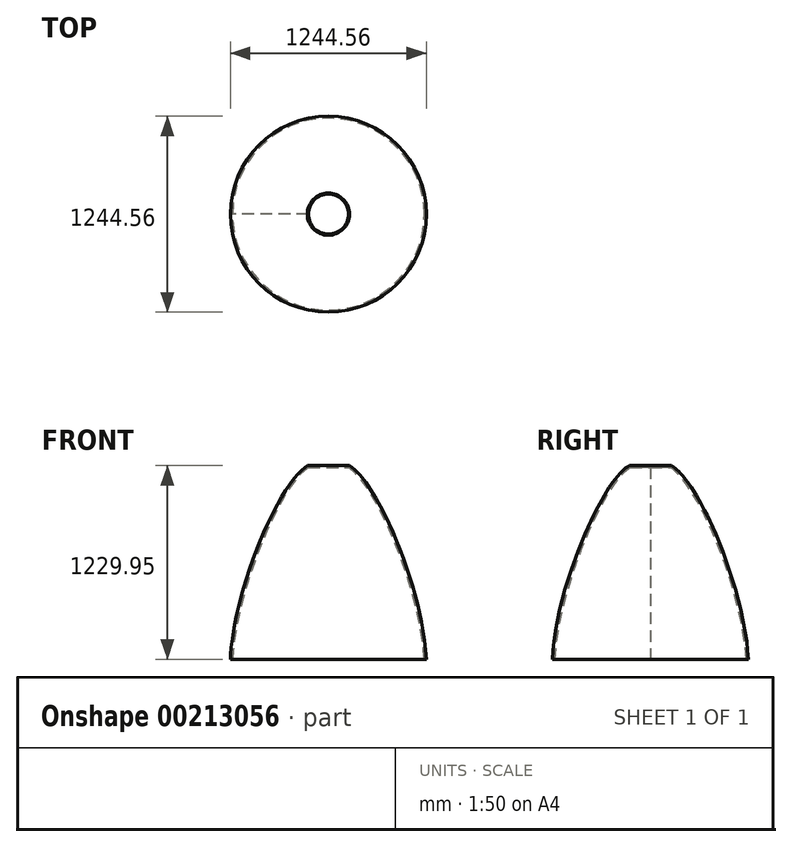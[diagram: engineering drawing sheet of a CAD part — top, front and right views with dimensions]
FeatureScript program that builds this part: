
annotation { "Feature Type Name" : "Feature", "Feature Type Description" : "" }
export const myFeature = defineFeature(function(context is Context, id is Id, definition is map)
    precondition{}
    {
        {
            var Q0;
            Q0=qCreatedBy(makeId("Front.planeOp"),FACE);
            var sketch = newSketch(context, id + "F0", { "sketchPlane" : qUnion([Q0])});
            skFitSpline(sketch, "E0", {"points": [v(-127, 0) * mm, v(-609.6, -1219.2) * mm], "startDerivative": vector(-564.76, -355.02) * mm, "endDerivative": vector(-64.8, -1241.7) * mm});
            skFitSpline(sketch, "E1.0", {"points": [v(-133.76, 10.75) * mm, v(-140.08, 6.78) * mm, v(-152.75, -2.27) * mm, v(-171.89, -18.92) * mm, v(-191.2, -38.5) * mm, v(-217.16, -68.32) * mm, v(-250, -112.2) * mm, v(-289.7, -174.32) * mm, v(-329.3, -244.7) * mm, v(-381.37, -347.98) * mm, v(-443.92, -491.79) * mm, v(-511.09, -678.15) * mm, v(-566.48, -868.55) * mm, v(-599.56, -1022.49) * mm, v(-616.2, -1137.97) * mm, v(-620.92, -1192.37) * mm, v(-622.28, -1218.54) * mm]});
            skLineSegment(sketch, "E2", {"start": v(-133.76, 10.75) * mm, "end": v(-127, 0) * mm});
            skLineSegment(sketch, "E3", {"start": v(-622.28, -1218.54) * mm, "end": v(-609.6, -1219.2) * mm});
            skLineSegment(sketch, "E4", {"start": v(0, 0) * mm, "end": v(0, 63.3) * mm});
            skSolve(sketch);
        }
        {
            var Q0;
            Q0=makeQuery(id+"F0.imprint","IMPRINT",FACE,{"disambiguationData":[TD([[makeQuery(id+"F0.imprint","IMPRINT",EDGE,{"derivedFrom":sQuery(id+"F0.wireOp",EDGE,"E0")}),-1.0]])]});
            var Q1;
            Q1=sQuery(id+"F0.wireOp",EDGE,"E4");
            revolve(context, id + "F1", {"entities" : qUnion([Q0]), "axis" : qUnion([Q1]), "revolveType" : RevolveType.FULL});
        }
    });
